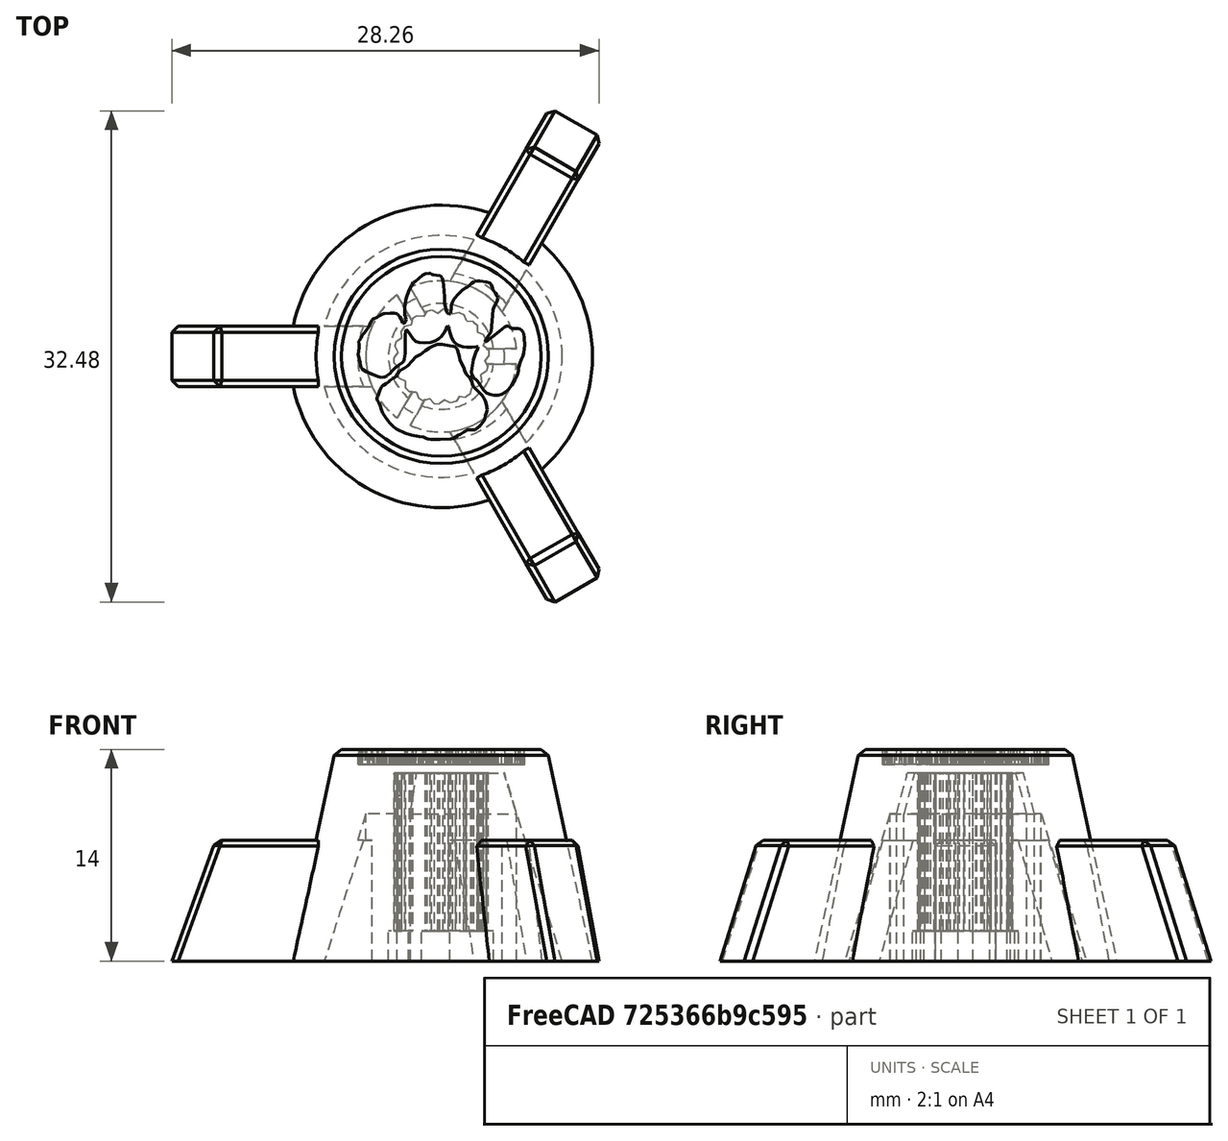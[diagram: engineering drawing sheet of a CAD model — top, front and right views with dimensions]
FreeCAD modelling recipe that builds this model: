
FCSTD DOCUMENT  (FreeCAD 0.18R14555 (Git shallow))
Label: lcd-knob-for-clone
License: All rights reserved
LicenseURL: http://en.wikipedia.org/wiki/All_rights_reserved
objects: Part::Feature×7, Part::Cut×5, Part::MultiCommon×3, Part::Cylinder×2, Part::Cone×2, Part::Box×2, Part::MultiFuse×1, Part::Chamfer×1
note: 23 computed .brp shape members not serialized (recipe doc carries the construction recipe); baked Part::Feature solids carry a one-line shape summary decoded from their .brp

FEATURE [Part::Feature] Powerful_Habbi001001_solid  label="hole"
  Placement = pos=(0.2,10.2,0) rot=(0,0,1;0rad)
  shape: bbox 7.502 x 7.501 x 12.43 mm, 81 faces (baked)
FEATURE [Part::Cylinder] Cylinder
  Angle = 360
  AttacherType = Attacher::AttachEngine3D
  Height = 17
  Radius = 3.5
FEATURE [Part::MultiCommon] Common  label="knob-hole"
  Shapes = -> [Cylinder,Powerful_Habbi001001_solid]
FEATURE [Part::Cone] Cone
  Angle = 360
  AttacherType = Attacher::AttachEngine3D
  Height = 14
  Radius1 = 10
  Radius2 = 7
FEATURE [Part::Cylinder] Cylinder001
  Angle = 360
  AttacherType = Attacher::AttachEngine3D
  Height = 13
  Radius = 5
FEATURE [Part::Cut] Cut
  Base = -> Cylinder001
  Tool = -> Common
FEATURE [Part::Cone] Cone001
  Angle = 360
  AttacherType = Attacher::AttachEngine3D
  Height = 13
  Radius1 = 8
  Radius2 = 4
FEATURE [Part::Cut] Cut001
  Base = -> Cone
  Tool = -> Cone001
FEATURE [Part::Box] Box  label="Cube"
  AttacherType = Attacher::AttachEngine3D
  Height = 12.43
  Length = 6
  Placement = pos=(0,-0.5,0) rot=(0,0,1;0rad)
  Width = 1
FEATURE [Part::Cut] Cut002
  Base = -> Cut
  Tool = -> Box
FEATURE [Part::Box] Box001  label="Cube001"
  AttacherType = Attacher::AttachEngine3D
  Height = 8
  Length = 14
  Placement = pos=(-18,-2,0) rot=(0,0,1;0rad)
  Width = 4
FEATURE [Part::Feature] Box002001  label="Cube003"
  Placement = pos=(0,0,2) rot=(0,0,1;0rad)
  shape: bbox 21.02 x 4 x 26.4 mm, 6 faces (baked)
FEATURE [Part::Cut] Cut003
  Base = -> Box001
  Tool = -> Box002001
FEATURE [Part::Feature] Cut003001  label="Cut004"
  Placement = pos=(0,0,0) rot=(0,0,-1;2.0944rad)
  shape: bbox 10.38 x 13.98 x 8 mm, 6 faces (baked)
FEATURE [Part::Feature] Cut003002  label="Cut005"
  Placement = pos=(0,0,0) rot=(0,0,1;2.0944rad)
  shape: bbox 10.38 x 13.98 x 8 mm, 6 faces (baked)
FEATURE [Part::Feature] Cool_Trug_Allis001001_solid  label="paw"
  Placement = pos=(3.5,3.5,13) rot=(0,0,1;0rad)
  shape: bbox 13 x 13 x 10 mm, 407 faces (baked)
FEATURE [Part::Feature] Cut002001  label="Cut006"
  Placement = pos=(0,0,0) rot=(0,0,1;4.18879rad)
  shape: bbox 10 x 10 x 13 mm, 63 faces (baked)
FEATURE [Part::Feature] Cut003003  label="Cut007"
  Placement = pos=(0,0,0) rot=(0,0,1;2.0944rad)
  shape: bbox 10 x 10 x 13 mm, 63 faces (baked)
FEATURE [Part::MultiCommon] Common001
  Shapes = -> [Cut003003,Cut002001]
FEATURE [Part::MultiCommon] Common002  label="core"
  Shapes = -> [Common001,Cut002]
FEATURE [Part::MultiFuse] Fusion
  Shapes = -> [Cut003002,Cut003001,Cut003,Cut001,Common002]
FEATURE [Part::Chamfer] Chamfer
  Base = -> Fusion
  Edges = 16 edges r=0.4: [Edge3,Edge4,Edge21,Edge22,Edge23,Edge24,Edge34,Edge35,Edge36,Edge37,Edge39,Edge44,Edge45,Edge46,Edge47,Edge49]
FEATURE [Part::Cut] Cut003004
  Base = -> Chamfer
  Tool = -> Cool_Trug_Allis001001_solid
